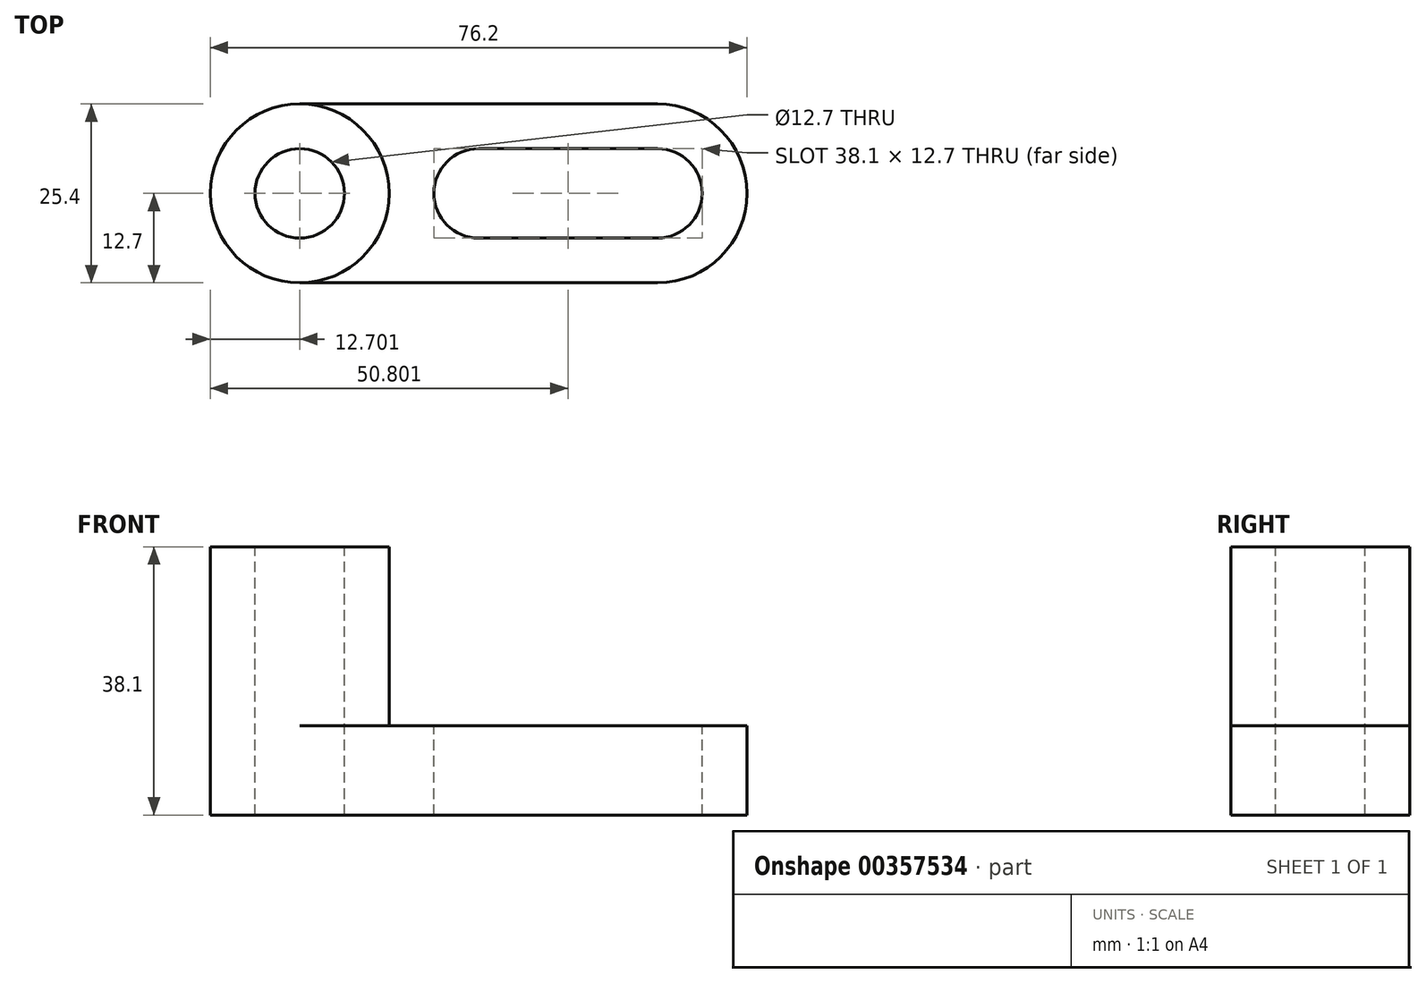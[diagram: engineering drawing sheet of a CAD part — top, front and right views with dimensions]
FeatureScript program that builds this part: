
annotation { "Feature Type Name" : "Feature", "Feature Type Description" : "" }
export const myFeature = defineFeature(function(context is Context, id is Id, definition is map)
    precondition{}
    {
        {
            var Q0;
            Q0=qCreatedBy(makeId("Front.planeOp"),FACE);
            var sketch = newSketch(context, id + "F0", { "sketchPlane" : qUnion([Q0])});
            skLineSegment(sketch, "E0.bottom", {"start": v(-38.72, -10.5) * mm, "end": v(37.48, -10.5) * mm});
            skLineSegment(sketch, "E0.top", {"start": v(-38.72, -23.2) * mm, "end": v(37.48, -23.2) * mm});
            skLineSegment(sketch, "E0.left", {"start": v(-38.72, -10.5) * mm, "end": v(-38.72, -23.2) * mm});
            skLineSegment(sketch, "E0.right", {"start": v(37.48, -10.5) * mm, "end": v(37.48, -23.2) * mm});
            skSolve(sketch);
        }
        {
            var Q0;
            Q0 = qSketchRegion(id + "F0", true);
            extrude(context, id + "F1", {"entities" : qUnion([Q0]), "depth" : 25.4 * mm});
        }
        {
            var Q0;
            Q0=makeQuery(id+"F1.opExtrude","SWEPT_FACE",FACE,{"disambiguationData":[OSD([sQuery(id+"F0.wireOp",EDGE,"E0.bottom")])]});
            var sketch = newSketch(context, id + "F2", { "sketchPlane" : qUnion([Q0])});
            skLineSegment(sketch, "E1", {"start": v(-26.02, 0) * mm, "end": v(24.78, 0) * mm});
            skLineSegment(sketch, "E2", {"start": v(37.48, -12.7) * mm, "end": v(37.48, -12.7) * mm});
            skLineSegment(sketch, "E3", {"start": v(24.78, -25.4) * mm, "end": v(-26.02, -25.4) * mm});
            skLineSegment(sketch, "E4", {"start": v(-38.72, -12.7) * mm, "end": v(-38.72, -12.7) * mm});
            skPoint(sketch, "E5.visualSharp", {"position": v(37.48, 0) * mm});
            skArc(sketch, "E5.filletArc", {"start": v(37.48, -12.7) * mm, "mid": v(33.76, -3.72) * mm, "end": v(24.78, 0) * mm});
            skPoint(sketch, "E6.visualSharp", {"position": v(37.48, -25.4) * mm});
            skArc(sketch, "E6.filletArc", {"start": v(24.78, -25.4) * mm, "mid": v(33.76, -21.68) * mm, "end": v(37.48, -12.7) * mm});
            skPoint(sketch, "E7.visualSharp", {"position": v(-38.72, 0) * mm});
            skArc(sketch, "E7.filletArc", {"start": v(-26.02, 0) * mm, "mid": v(-35, -3.72) * mm, "end": v(-38.72, -12.7) * mm});
            skPoint(sketch, "E8.visualSharp", {"position": v(-38.72, -25.4) * mm});
            skArc(sketch, "E8.filletArc", {"start": v(-38.72, -12.7) * mm, "mid": v(-35, -21.68) * mm, "end": v(-26.02, -25.4) * mm});
            skSolve(sketch);
        }
        {
            var Q0;
            {var subQ0=sQuery(id+"F2.wireOp",EDGE,"E7.filletArc");Q0=makeQuery(id+"F2.imprint","IMPRINT",FACE,{"disambiguationData":[TD([[makeQuery(id+"F2.imprint","IMPRINT",EDGE,{"derivedFrom":subQ0}),-1.0]])]});}
            var Q1;
            {var subQ0=sQuery(id+"F2.wireOp",EDGE,"E8.filletArc");Q1=makeQuery(id+"F2.imprint","IMPRINT",FACE,{"disambiguationData":[TD([[makeQuery(id+"F2.imprint","IMPRINT",EDGE,{"derivedFrom":subQ0}),-1.0]])]});}
            var Q2;
            {var subQ0=sQuery(id+"F2.wireOp",EDGE,"E6.filletArc");Q2=makeQuery(id+"F2.imprint","IMPRINT",FACE,{"disambiguationData":[TD([[makeQuery(id+"F2.imprint","IMPRINT",EDGE,{"derivedFrom":subQ0}),-1.0]])]});}
            var Q3;
            {var subQ0=sQuery(id+"F2.wireOp",EDGE,"E5.filletArc");Q3=makeQuery(id+"F2.imprint","IMPRINT",FACE,{"disambiguationData":[TD([[makeQuery(id+"F2.imprint","IMPRINT",EDGE,{"derivedFrom":subQ0}),-1.0]])]});}
            extrude(context, id + "F3", {"entities" : qUnion([Q0, Q1, Q2, Q3]), "operationType" : NewBodyOperationType.REMOVE, "oppositeDirection" : true, "depth" : 12.7 * mm});
        }
        {
            var Q0;
            Q0=makeQuery(id+"F1.opExtrude","SWEPT_FACE",FACE,{"disambiguationData":[OSD([sQuery(id+"F0.wireOp",EDGE,"E0.bottom")])]});
            var sketch = newSketch(context, id + "F4", { "sketchPlane" : qUnion([Q0])});
            skCircle(sketch, "E9", {"center": v(-26.02, -12.7) * mm, "radius": 12.7 * mm});
            skSolve(sketch);
        }
        {
            var Q0;
            {var subQ0=sQuery(id+"F4.wireOp",EDGE,"E9");var subQ1=sQuery(id+"F0.wireOp",EDGE,"E0.bottom");var subQ2=makeQuery(id+"F4.imprint","INTERSECT",VERTEX,{"derivedFrom":[makeQuery(id+"F1.opExtrude","CAP_EDGE",EDGE,{"disambiguationData":[OSD([subQ1])],"isStart":true}),subQ0]});Q0=makeQuery(id+"F4.imprint","IMPRINT",FACE,{"disambiguationData":[TD([[makeQuery(id+"F4.imprint","IMPRINT",EDGE,{"disambiguationData":[TD([[subQ2,1.0]])],"derivedFrom":subQ0}),1.0]])]});}
            extrude(context, id + "F5", {"entities" : qUnion([Q0]), "operationType" : NewBodyOperationType.ADD, "depth" : 25.4 * mm});
        }
        {
            var Q0;
            Q0=makeQuery(id+"F5.opExtrude","CAP_FACE",FACE,{"disambiguationData":[OSD([sQuery(id+"F4.wireOp",EDGE,"E9")])],"isStart":false});
            var sketch = newSketch(context, id + "F6", { "sketchPlane" : qUnion([Q0])});
            skCircle(sketch, "E10", {"center": v(-26.02, -12.7) * mm, "radius": 6.35 * mm});
            skSolve(sketch);
        }
        {
            var Q0;
            Q0=makeQuery(id+"F6.imprint","IMPRINT",FACE,{"disambiguationData":[TD([[makeQuery(id+"F6.imprint","IMPRINT",EDGE,{"derivedFrom":sQuery(id+"F6.wireOp",EDGE,"E10")}),1.0]])]});
            extrude(context, id + "F7", {"entities" : qUnion([Q0]), "operationType" : NewBodyOperationType.REMOVE, "oppositeDirection" : true, "depth" : 38.1 * mm});
        }
        {
            var Q0;
            Q0=makeQuery(id+"F1.opExtrude","SWEPT_FACE",FACE,{"disambiguationData":[OSD([sQuery(id+"F0.wireOp",EDGE,"E0.bottom")])]});
            var sketch = newSketch(context, id + "F8", { "sketchPlane" : qUnion([Q0])});
            skLineSegment(sketch, "E11", {"start": v(37.48, -12.7) * mm, "end": v(31.13, -12.7) * mm});
            skPoint(sketch, "E11.endSnap0", {"position": v(37.48, -12.7) * mm});
            skLineSegment(sketch, "E12", {"start": v(-13.32, -12.7) * mm, "end": v(-6.97, -12.7) * mm});
            skLineSegment(sketch, "E13", {"start": v(-0.62, -19.05) * mm, "end": v(24.78, -19.05) * mm});
            skLineSegment(sketch, "E14", {"start": v(31.13, -19.05) * mm, "end": v(31.13, -12.7) * mm});
            skLineSegment(sketch, "E15", {"start": v(24.78, -6.35) * mm, "end": v(-0.62, -6.35) * mm});
            skLineSegment(sketch, "E16", {"start": v(-6.97, -6.35) * mm, "end": v(-6.97, -12.7) * mm});
            skLineSegment(sketch, "E17", {"start": v(31.13, -12.7) * mm, "end": v(31.13, -6.35) * mm});
            skLineSegment(sketch, "E18", {"start": v(31.13, -12.7) * mm, "end": v(31.13, -12.7) * mm});
            skLineSegment(sketch, "E19", {"start": v(-6.97, -12.7) * mm, "end": v(-6.97, -12.7) * mm});
            skPoint(sketch, "E20.visualSharp", {"position": v(-6.97, -6.35) * mm});
            skArc(sketch, "E20.filletArc", {"start": v(-0.62, -6.35) * mm, "mid": v(-5.1, -8.2) * mm, "end": v(-6.97, -12.7) * mm});
            skPoint(sketch, "E21.visualSharp", {"position": v(-6.97, -19.05) * mm});
            skArc(sketch, "E21.filletArc", {"start": v(-6.97, -12.7) * mm, "mid": v(-5.1, -17.2) * mm, "end": v(-0.62, -19.05) * mm});
            skPoint(sketch, "E22.visualSharp", {"position": v(31.13, -6.35) * mm});
            skArc(sketch, "E22.filletArc", {"start": v(31.13, -12.7) * mm, "mid": v(29.27, -8.2) * mm, "end": v(24.78, -6.35) * mm});
            skPoint(sketch, "E23.visualSharp", {"position": v(31.13, -19.05) * mm});
            skArc(sketch, "E23.filletArc", {"start": v(24.78, -19.05) * mm, "mid": v(29.27, -17.2) * mm, "end": v(31.13, -12.7) * mm});
            skSolve(sketch);
        }
        {
            var Q0;
            Q0 = qSketchRegion(id + "F8", true);
            extrude(context, id + "F9", {"entities" : qUnion([Q0]), "operationType" : NewBodyOperationType.REMOVE, "oppositeDirection" : true, "depth" : 12.7 * mm});
        }
    });
